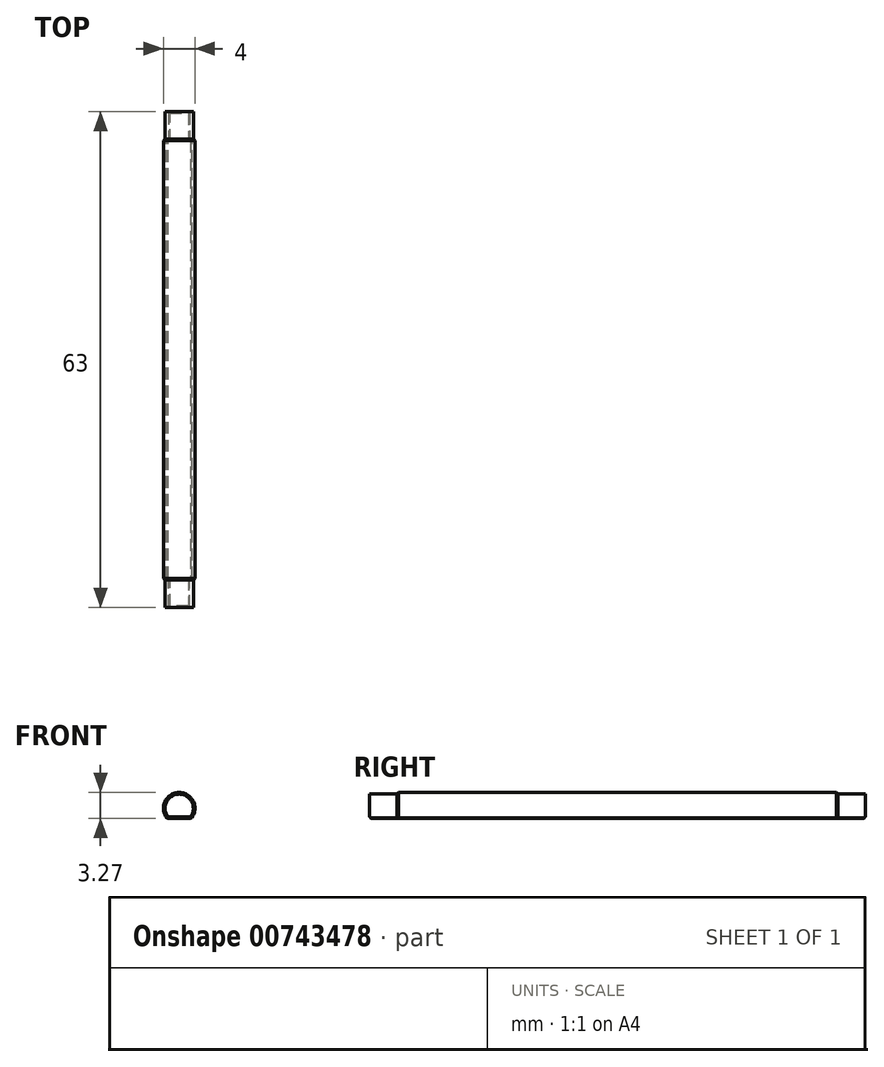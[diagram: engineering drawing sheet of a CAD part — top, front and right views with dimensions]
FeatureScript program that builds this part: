
annotation { "Feature Type Name" : "Feature", "Feature Type Description" : "" }
export const myFeature = defineFeature(function(context is Context, id is Id, definition is map)
    precondition{}
    {
        {
            assignVariable(context, id + "F0", {"name" : "pinLength", "anyValue" : 56});
        }
        {
            assignVariable(context, id + "F1", {"name" : "insertLength", "anyValue" : 3.5});
        }
        {
            var Q0;
            Q0=qCreatedBy(makeId("Front.planeOp"),FACE);
            var sketch = newSketch(context, id + "F2", { "sketchPlane" : qUnion([Q0])});
            skCircle(sketch, "E0", {"center": v(0, 0) * mm, "radius": 2 * mm});
            skSolve(sketch);
        }
        {
            var Q0;
            Q0=makeQuery(id+"F2.imprint","IMPRINT",FACE,{"disambiguationData":[TD([[makeQuery(id+"F2.imprint","IMPRINT",EDGE,{"derivedFrom":sQuery(id+"F2.wireOp",EDGE,"E0")}),1.0]])]});
            extrude(context, id + "F3", {"entities" : qUnion([Q0]), "depth" : (getVariable(context, 'pinLength') / 2) * mm, "offsetDistance" : 25 * mm});
        }
        {
            var Q0;
            Q0=makeQuery(id+"F3.opExtrude","CAP_FACE",FACE,{"disambiguationData":[OSD([sQuery(id+"F2.wireOp",EDGE,"E0")])],"isStart":false});
            var sketch = newSketch(context, id + "F4", { "sketchPlane" : qUnion([Q0])});
            skCircle(sketch, "E1", {"center": v(0, 0) * mm, "radius": 1.8 * mm});
            skSolve(sketch);
        }
        {
            var Q0;
            Q0=makeQuery(id+"F4.imprint","IMPRINT",FACE,{"disambiguationData":[TD([[makeQuery(id+"F4.imprint","IMPRINT",EDGE,{"derivedFrom":sQuery(id+"F4.wireOp",EDGE,"E1")}),1.0]])]});
            extrude(context, id + "F5", {"entities" : qUnion([Q0]), "operationType" : NewBodyOperationType.ADD, "depth" : (getVariable(context, 'insertLength')) * mm, "offsetDistance" : 25 * mm});
        }
        {
            var Q0;
            Q0=makeQuery(id+"F3.opExtrude","SWEPT_BODY",BODY,{"disambiguationData":[OSD([sQuery(id+"F2.wireOp",EDGE,"E0")])]});
            var Q1;
            Q1=makeQuery(id+"F3.opExtrude","CAP_FACE",FACE,{"disambiguationData":[OSD([sQuery(id+"F2.wireOp",EDGE,"E0")])],"isStart":true});
            mirror(context, id + "F6", {"operationType" : NewBodyOperationType.ADD, "entities" : qUnion([Q0]), "mirrorPlane" : qUnion([Q1])});
        }
        {
            var Q0;
            Q0=qCreatedBy(makeId("Front.planeOp"),FACE);
            var sketch = newSketch(context, id + "F7", { "sketchPlane" : qUnion([Q0])});
            skLineSegment(sketch, "E2.bottom", {"start": v(-1.54, -1.27) * mm, "end": v(1.54, -1.27) * mm});
            skLineSegment(sketch, "E2.top", {"start": v(-1.54, -2) * mm, "end": v(1.54, -2) * mm});
            skLineSegment(sketch, "E2.left", {"start": v(-1.54, -1.27) * mm, "end": v(-1.54, -2) * mm});
            skLineSegment(sketch, "E2.right", {"start": v(1.54, -1.27) * mm, "end": v(1.54, -2) * mm});
            skCircle(sketch, "E3.0", {"center": v(0, 0) * mm, "radius": 1.8 * mm, "construction": true});
            skLineSegment(sketch, "E4", {"start": v(-1.27, -1.27) * mm, "end": v(-1.84, -0.7) * mm, "construction": true});
            skSolve(sketch);
        }
        {
            var Q0;
            Q0=makeQuery(id+"F7.imprint","IMPRINT",FACE,{"disambiguationData":[TD([[makeQuery(id+"F7.imprint","IMPRINT",EDGE,{"derivedFrom":sQuery(id+"F7.wireOp",EDGE,"E2.bottom")}),-1.0]])]});
            extrude(context, id + "F8", {"entities" : qUnion([Q0]), "operationType" : NewBodyOperationType.REMOVE, "endBound" : BoundingType.THROUGH_ALL, "oppositeDirection" : true, "depth" : 25 * mm, "offsetDistance" : 25 * mm, "hasSecondDirection" : true, "secondDirectionBound" : SecondDirectionBoundingType.THROUGH_ALL, "secondDirectionOppositeDirection" : false, "secondDirectionDepth" : 25 * mm});
        }
        {
            var Q0;
            Q0=makeQuery(id+"F8.boolean.opBoolean","COPY",FACE,{"derivedFrom":makeQuery(id+"F8.opExtrude","SWEPT_FACE",FACE,{"disambiguationData":[OSD([sQuery(id+"F7.wireOp",EDGE,"E2.bottom")])]})});
            chamfer(context, id + "F9", {"entities" : qUnion([Q0]), "width" : 0.2 * mm, "tangentPropagation" : true});
        }
        {
            var Q0;
            Q0=makeQuery(id+"F3.opExtrude","CAP_EDGE",EDGE,{"disambiguationData":[OSD([sQuery(id+"F2.wireOp",EDGE,"E0")])],"isStart":false});
            var Q1;
            Q1=makeQuery(id+"F6.opPattern","COPY",EDGE,{"derivedFrom":makeQuery(id+"F3.opExtrude","CAP_EDGE",EDGE,{"disambiguationData":[OSD([sQuery(id+"F2.wireOp",EDGE,"E0")])],"isStart":false}),"instanceName":"1"});
            chamfer(context, id + "F10", {"entities" : qUnion([Q0, Q1]), "width" : 0.2 * mm, "tangentPropagation" : true});
        }
    });
